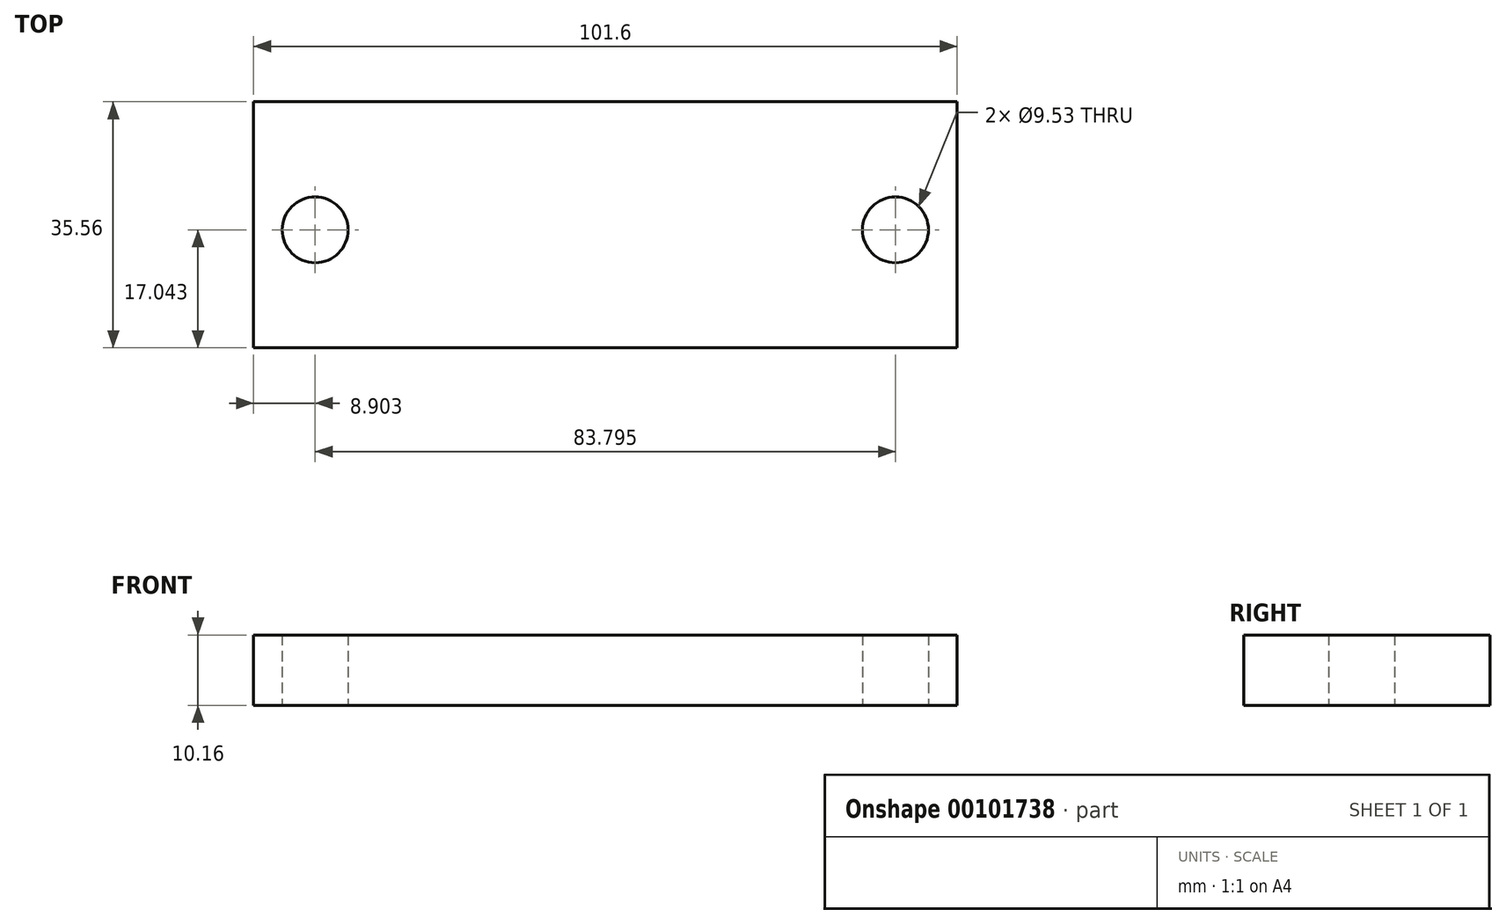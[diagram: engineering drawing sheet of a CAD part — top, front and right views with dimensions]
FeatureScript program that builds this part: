
annotation { "Feature Type Name" : "Feature", "Feature Type Description" : "" }
export const myFeature = defineFeature(function(context is Context, id is Id, definition is map)
    precondition{}
    {
        {
            var Q0;
            Q0=qCreatedBy(makeId("Top.planeOp"),FACE);
            var sketch = newSketch(context, id + "F0", { "sketchPlane" : qUnion([Q0])});
            skLineSegment(sketch, "E0.bottom", {"start": v(0, 0) * mm, "end": v(101.6, 0) * mm});
            skLineSegment(sketch, "E0.top", {"start": v(0, 35.56) * mm, "end": v(101.6, 35.56) * mm});
            skLineSegment(sketch, "E0.left", {"start": v(0, 0) * mm, "end": v(0, 35.56) * mm});
            skLineSegment(sketch, "E0.right", {"start": v(101.6, 0) * mm, "end": v(101.6, 35.56) * mm});
            skCircle(sketch, "E1", {"center": v(8.9, 17.04) * mm, "radius": 4.76 * mm});
            skCircle(sketch, "E2", {"center": v(92.7, 17.04) * mm, "radius": 4.76 * mm});
            skSolve(sketch);
        }
        {
            var Q0;
            Q0=qSketchRegion(id+"F0",true);
            extrude(context, id + "F1", {"entities" : qUnion([Q0]), "depth" : 10.16 * mm});
        }
    });
